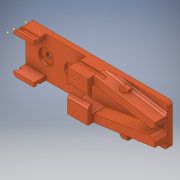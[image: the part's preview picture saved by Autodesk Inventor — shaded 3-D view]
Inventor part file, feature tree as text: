
AUTODESK INVENTOR PART (.ipt)
format: ipt  version: 2017 (Build 210142000, 142)  size: 439,296 bytes
history: native  units: in
note: dims shown in document units (in); Inventor stores cm internally (conversion verified against a paired STEP export)
features: sketch x27, extrude x23, mirror x5, plane x4, fillet x2
ambient origin geometry x8: Origin, YZ Plane, XZ Plane, XY Plane, X Axis, Y Axis, Z Axis, Center Point
bodies: Solid1 (feature_tree)
feature tree (61):
  extrude  "Extrusion1"  Depth=1.0in
  extrude  "Extrusion2"  Depth=0.5in
  plane  "Work Plane2"
  mirror  "Mirror2"
  extrude  "Extrusion4"  Depth=0.5in
  mirror  "Mirror3"
  extrude  "Extrusion5"  Depth=0.375in TaperAngle=0.0deg
  extrude  "Extrusion6"  Depth=0.1875in
  extrude  "Extrusion7"  Depth=0.15in
  extrude  "Extrusion8"  Depth=0.15in TaperAngle=0.0deg
  extrude  "Extrusion9"  Depth=0.25in
  extrude  "Extrusion11"  Depth=0.2in TaperAngle=0.0deg
  sketch  "Sketch12"  dims[d27=1.0in d28=0.0in d29=0.375in]
  extrude  "Extrusion12"  Depth=0.375in
  extrude  "Extrusion13"  Depth=0.125in
  extrude  "Extrusion14"  Depth=1.0in TaperAngle=0.0deg
  sketch  "Sketch16"  dims[d43=0.4375in d44=0.4375in d45=0.3125in d46=0.0in]
  sketch  "Sketch17"  dims[d47=0.05in d48=0.0in d49=0.1in d50=0.0in]
  extrude  "Extrusion15"  Depth=1.0in TaperAngle=0.0deg
  extrude  "Extrusion16"  Depth=0.4375in
  fillet  "Fillet1"  Radius=0.3125in
  extrude  "Extrusion17"  Depth=0.1in TaperAngle=0.0deg
  extrude  "Extrusion18"  Depth=1.0in TaperAngle=0.0deg
  plane  "Work Plane4"
  mirror  "Mirror4"
  extrude  "Extrusion19"  Depth=3.0in TaperAngle=0.0deg
  plane  "Work Plane5"
  mirror  "Mirror5"
  extrude  "Extrusion20"  Depth=0.1in
  extrude  "Extrusion21"  Depth=0.1in TaperAngle=0.0deg
  mirror  "Mirror6"
  extrude  "Extrusion22"  Depth=0.1in TaperAngle=0.0deg
  sketch  "Sketch26"
  extrude  "Extrusion23"  Depth=0.0625in TaperAngle=0.0deg
  extrude  "Extrusion24"  Depth=0.0625in TaperAngle=0.0deg
  extrude  "Extrusion25"  Depth=0.075in
  fillet  "Fillet2"  [1 undecoded]
  sketch  "Sketch1"  dims[d0=2.5in d1=1.0in]
  sketch  "Sketch2"  dims[d2=0.125in d3=0.0in d4=0.5in]
  plane  "Work Plane3"
  sketch  "Sketch4"  dims[d5=0.1in d6=0.5in]
  sketch  "Sketch5"  dims[d7=0.1875in d8=0.375in d9=0.0in]
  sketch  "Sketch6"  dims[d13=0.5in d14=0.1875in]
  sketch  "Sketch7"  dims[d15=0.3125in d16=0.0in d17=0.15in]
  sketch  "Sketch8"  dims[d18=0.15in d19=0.15in d20=0.0in]
  sketch  "Sketch9"  dims[d21=0.5in d22=0.0in d23=0.25in]
  sketch  "Sketch11"  dims[d24=0.25in d25=0.2in d26=0.0in]
  sketch  "Sketch13"  dims[d30=0.0625in d31=0.0in d35=0.125in]
  sketch  "Sketch14"  dims[d36=0.125in d37=1.0in d38=0.0in]
  sketch  "Sketch15"  dims[d39=3.0in d40=0.0in d41=1.0in d42=0.0in]
  sketch  "Sketch18"  dims[d51=0.125in d52=1.0in d53=0.0in]
  sketch  "Sketch19"  dims[d54=1.0in d55=0.0in d56=3.0in d57=0.0in]
  sketch  "Sketch20"  dims[d58=0.1in d59=0.1in]
  sketch  "Sketch21"  dims[d60=0.15in d61=0.0in d62=0.1in d63=0.0in]
  sketch  "Sketch22"  dims[d64=0.1in d65=0.0in d66=0.1in d67=0.0in]
  sketch  "Sketch23"  dims[d68=0.365in d69=0.0625in d70=0.0in]
  sketch  "Sketch24"  dims[d71=0.125in d72=0.0625in d73=0.0in]
  sketch  "Sketch25"  dims[d74=0.075in d75=0.075in]
  sketch  "Sketch27"
  sketch  "Sketch28"
  sketch  "Sketch29"
note: 1 required parameter value undecoded (feature->parameter linkage not recoverable at this tier; creation-order binding heuristic only, values carry confidence <= 0.55)
